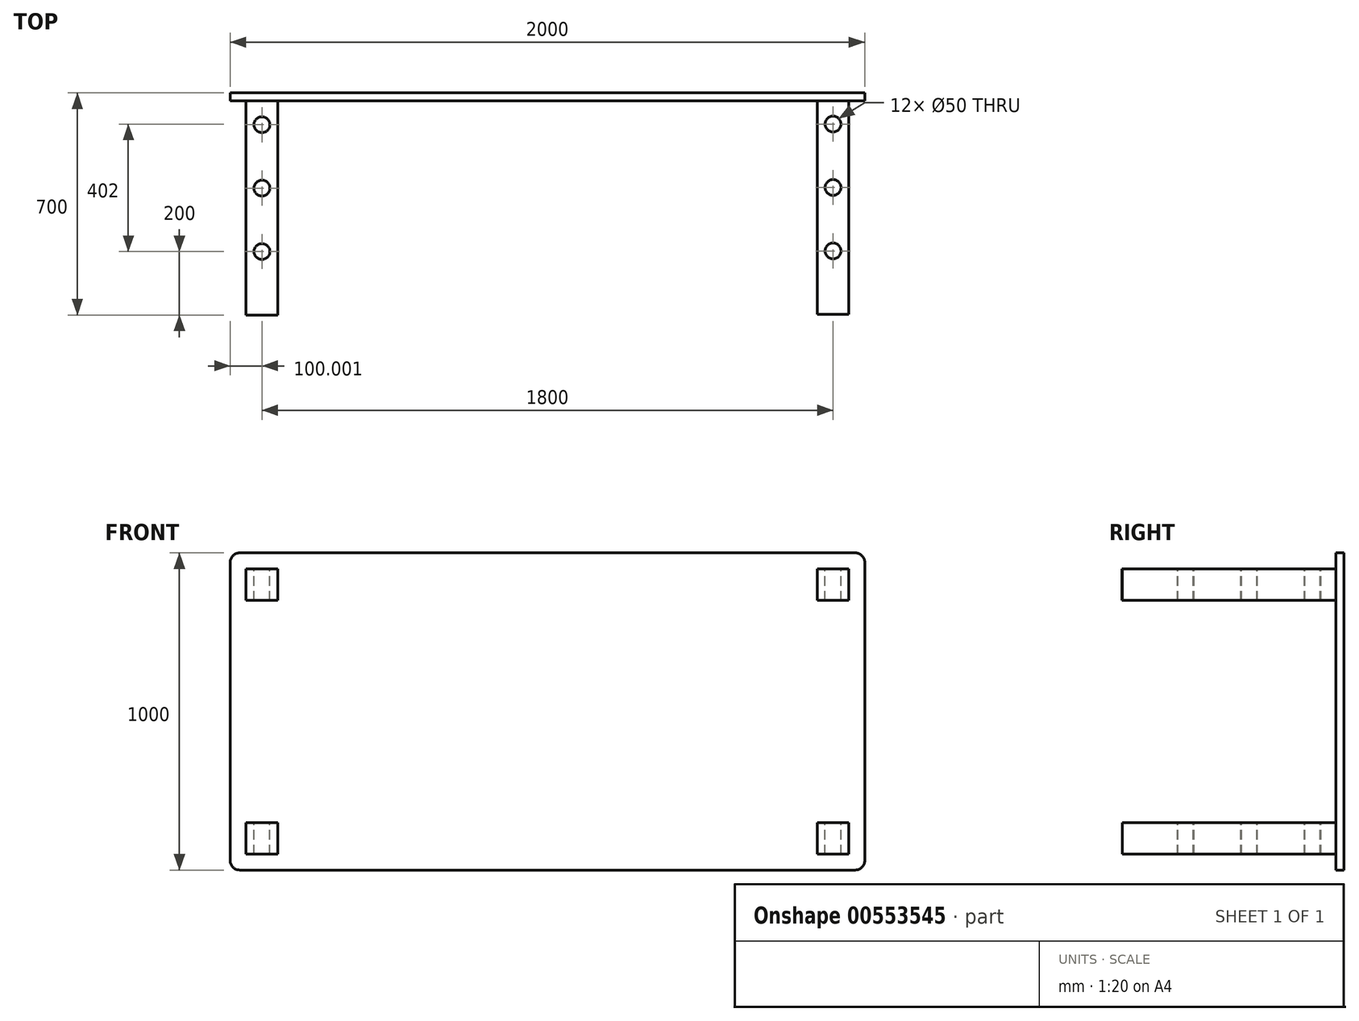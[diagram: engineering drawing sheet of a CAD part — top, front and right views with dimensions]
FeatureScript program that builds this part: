
annotation { "Feature Type Name" : "Feature", "Feature Type Description" : "" }
export const myFeature = defineFeature(function(context is Context, id is Id, definition is map)
    precondition{}
    {
        {
            var Q0;
            Q0=qCreatedBy(makeId("Front.planeOp"),FACE);
            var sketch = newSketch(context, id + "F0", { "sketchPlane" : qUnion([Q0])});
            skLineSegment(sketch, "E0.bottom", {"start": v(-998.7, 511.5) * mm, "end": v(1001.3, 511.5) * mm});
            skLineSegment(sketch, "E0.top", {"start": v(-998.7, -488.5) * mm, "end": v(1001.3, -488.5) * mm});
            skLineSegment(sketch, "E0.left", {"start": v(-998.7, 511.5) * mm, "end": v(-998.7, -488.5) * mm});
            skLineSegment(sketch, "E0.right", {"start": v(1001.3, 511.5) * mm, "end": v(1001.3, -488.5) * mm});
            skSolve(sketch);
        }
        {
            var Q0;
            Q0 = qSketchRegion(id + "F0", true);
            extrude(context, id + "F1", {"entities" : qUnion([Q0]), "depth" : 25 * mm, "offsetDistance" : 25 * mm});
        }
        {
            var Q0;
            Q0=qCreatedBy(makeId("Front.planeOp"),FACE);
            var sketch = newSketch(context, id + "F2", { "sketchPlane" : qUnion([Q0])});
            skLineSegment(sketch, "E1.bottom", {"start": v(-948.7, 461.5) * mm, "end": v(-848.7, 461.5) * mm});
            skLineSegment(sketch, "E1.top", {"start": v(-948.7, 361.5) * mm, "end": v(-848.7, 361.5) * mm});
            skLineSegment(sketch, "E1.left", {"start": v(-948.7, 461.5) * mm, "end": v(-948.7, 361.5) * mm});
            skLineSegment(sketch, "E1.right", {"start": v(-848.7, 461.5) * mm, "end": v(-848.7, 361.5) * mm});
            skSolve(sketch);
        }
        {
            var Q0;
            Q0 = qSketchRegion(id + "F2", true);
            extrude(context, id + "F3", {"entities" : qUnion([Q0]), "operationType" : NewBodyOperationType.ADD, "depth" : 700 * mm, "offsetDistance" : 25 * mm});
        }
        {
            var Q0;
            Q0=makeQuery(id+"F3.opExtrude","SWEPT_FACE",FACE,{"disambiguationData":[OSD([sQuery(id+"F2.wireOp",EDGE,"E1.bottom")])]});
            var sketch = newSketch(context, id + "F4", { "sketchPlane" : qUnion([Q0])});
            skCircle(sketch, "E2", {"center": v(-898.7, -500) * mm, "radius": 25 * mm});
            skSolve(sketch);
        }
        {
            var Q0;
            Q0=makeQuery(id+"F1.opExtrude","CAP_FACE",FACE,{"disambiguationData":[OSD([sQuery(id+"F0.wireOp",EDGE,"E0.bottom"),sQuery(id+"F0.wireOp",EDGE,"E0.top"),sQuery(id+"F0.wireOp",EDGE,"E0.left"),sQuery(id+"F0.wireOp",EDGE,"E0.right")])],"isStart":false});
            var sketch = newSketch(context, id + "F5", { "sketchPlane" : qUnion([Q0])});
            skLineSegment(sketch, "E3.bottom", {"start": v(951.3, 461.5) * mm, "end": v(851.3, 461.5) * mm});
            skLineSegment(sketch, "E3.top", {"start": v(951.3, 361.5) * mm, "end": v(851.3, 361.5) * mm});
            skLineSegment(sketch, "E3.left", {"start": v(951.3, 461.5) * mm, "end": v(951.3, 361.5) * mm});
            skLineSegment(sketch, "E3.right", {"start": v(851.3, 461.5) * mm, "end": v(851.3, 361.5) * mm});
            skLineSegment(sketch, "E4.bottom", {"start": v(-948.7, -438.5) * mm, "end": v(-848.7, -438.5) * mm});
            skLineSegment(sketch, "E4.top", {"start": v(-948.7, -338.5) * mm, "end": v(-848.7, -338.5) * mm});
            skLineSegment(sketch, "E4.left", {"start": v(-948.7, -438.5) * mm, "end": v(-948.7, -338.5) * mm});
            skLineSegment(sketch, "E4.right", {"start": v(-848.7, -438.5) * mm, "end": v(-848.7, -338.5) * mm});
            skLineSegment(sketch, "E5.bottom", {"start": v(951.3, -438.5) * mm, "end": v(851.3, -438.5) * mm});
            skLineSegment(sketch, "E5.top", {"start": v(951.3, -338.5) * mm, "end": v(851.3, -338.5) * mm});
            skLineSegment(sketch, "E5.left", {"start": v(951.3, -438.5) * mm, "end": v(951.3, -338.5) * mm});
            skLineSegment(sketch, "E5.right", {"start": v(851.3, -438.5) * mm, "end": v(851.3, -338.5) * mm});
            skSolve(sketch);
        }
        {
            var Q0;
            Q0=makeQuery(id+"F5.imprint","IMPRINT",FACE,{"disambiguationData":[TD([[makeQuery(id+"F5.imprint","IMPRINT",EDGE,{"derivedFrom":sQuery(id+"F5.wireOp",EDGE,"E4.bottom")}),1.0]])]});
            var Q1;
            Q1=makeQuery(id+"F5.imprint","IMPRINT",FACE,{"disambiguationData":[TD([[makeQuery(id+"F5.imprint","IMPRINT",EDGE,{"derivedFrom":sQuery(id+"F5.wireOp",EDGE,"E5.bottom")}),-1.0]])]});
            var Q2;
            Q2=makeQuery(id+"F5.imprint","IMPRINT",FACE,{"disambiguationData":[TD([[makeQuery(id+"F5.imprint","IMPRINT",EDGE,{"derivedFrom":sQuery(id+"F5.wireOp",EDGE,"E3.bottom")}),1.0]])]});
            extrude(context, id + "F6", {"entities" : qUnion([Q0, Q1, Q2]), "operationType" : NewBodyOperationType.ADD, "depth" : 673 * mm, "offsetDistance" : 25 * mm});
        }
        {
            var Q0;
            Q0=sQuery(id+"F4.wireOp",VERTEX,"E2.center");
            var Q1;
            Q1=makeQuery(id+"F1.opExtrude","SWEPT_BODY",BODY,{"disambiguationData":[OSD([sQuery(id+"F0.wireOp",EDGE,"E0.bottom"),sQuery(id+"F0.wireOp",EDGE,"E0.top"),sQuery(id+"F0.wireOp",EDGE,"E0.left"),sQuery(id+"F0.wireOp",EDGE,"E0.right")])]});
            hole(context, id + "F7", {"style" : HoleStyle.SIMPLE, "endStyle" : HoleEndStyle.THROUGH, "holeDiameter" : 50 * mm, "isTappedThrough" : true, "tappedDepth" : 12 * mm, "tapClearance" : 3, "locations" : qUnion([Q0]), "scope" : qUnion([Q1])});
        }
        {
            var Q0;
            Q0=makeQuery(id+"F3.opExtrude","SWEPT_FACE",FACE,{"disambiguationData":[OSD([sQuery(id+"F2.wireOp",EDGE,"E1.bottom")])]});
            var sketch = newSketch(context, id + "F8", { "sketchPlane" : qUnion([Q0])});
            skCircle(sketch, "E6", {"center": v(-898.7, -300) * mm, "radius": 25 * mm});
            skCircle(sketch, "E7", {"center": v(-898.7, -100) * mm, "radius": 25 * mm});
            skCircle(sketch, "E8", {"center": v(-898.7, -500) * mm, "radius": 25 * mm});
            skCircle(sketch, "E9", {"center": v(901.3, -498) * mm, "radius": 25 * mm});
            skCircle(sketch, "E10", {"center": v(901.3, -298) * mm, "radius": 25 * mm});
            skCircle(sketch, "E11", {"center": v(901.3, -98) * mm, "radius": 25 * mm});
            skSolve(sketch);
        }
        {
            var Q0;
            Q0 = qSketchRegion(id + "F8", true);
            extrude(context, id + "F9", {"entities" : qUnion([Q0]), "operationType" : NewBodyOperationType.ADD, "depth" : 25 * mm, "offsetDistance" : 25 * mm});
        }
        {
            var Q0;
            Q0=makeQuery(id+"F9.opExtrude","CAP_FACE",FACE,{"disambiguationData":[OSD([sQuery(id+"F8.wireOp",EDGE,"E6")])],"isStart":false});
            var Q1;
            Q1=makeQuery(id+"F9.opExtrude","CAP_FACE",FACE,{"disambiguationData":[OSD([sQuery(id+"F8.wireOp",EDGE,"E7")])],"isStart":false});
            var Q2;
            Q2=makeQuery(id+"F9.opExtrude","CAP_FACE",FACE,{"disambiguationData":[OSD([sQuery(id+"F8.wireOp",EDGE,"E8")])],"isStart":false});
            var Q3;
            Q3=makeQuery(id+"F9.opExtrude","CAP_FACE",FACE,{"disambiguationData":[OSD([sQuery(id+"F8.wireOp",EDGE,"E11")])],"isStart":false});
            var Q4;
            Q4=makeQuery(id+"F9.opExtrude","CAP_FACE",FACE,{"disambiguationData":[OSD([sQuery(id+"F8.wireOp",EDGE,"E10")])],"isStart":false});
            var Q5;
            Q5=makeQuery(id+"F9.opExtrude","CAP_FACE",FACE,{"disambiguationData":[OSD([sQuery(id+"F8.wireOp",EDGE,"E9")])],"isStart":false});
            extrude(context, id + "F10", {"entities" : qUnion([Q0, Q1, Q2, Q3, Q4, Q5]), "operationType" : NewBodyOperationType.REMOVE, "endBound" : BoundingType.THROUGH_ALL, "oppositeDirection" : true, "depth" : 25 * mm, "offsetDistance" : 25 * mm});
        }
        {
            var Q0;
            Q0=makeQuery(id+"F1.opExtrude","SWEPT_EDGE",EDGE,{"disambiguationData":[OSD([sQuery(id+"F0.wireOp",EDGE,"E0.bottom"),sQuery(id+"F0.wireOp",EDGE,"E0.left")])]});
            var Q1;
            Q1=makeQuery(id+"F1.opExtrude","SWEPT_EDGE",EDGE,{"disambiguationData":[OSD([sQuery(id+"F0.wireOp",EDGE,"E0.top"),sQuery(id+"F0.wireOp",EDGE,"E0.left")])]});
            var Q2;
            Q2=makeQuery(id+"F1.opExtrude","SWEPT_EDGE",EDGE,{"disambiguationData":[OSD([sQuery(id+"F0.wireOp",EDGE,"E0.top"),sQuery(id+"F0.wireOp",EDGE,"E0.right")])]});
            var Q3;
            Q3=makeQuery(id+"F1.opExtrude","SWEPT_EDGE",EDGE,{"disambiguationData":[OSD([sQuery(id+"F0.wireOp",EDGE,"E0.bottom"),sQuery(id+"F0.wireOp",EDGE,"E0.right")])]});
            fillet(context, id + "F11", {"entities" : qUnion([Q0, Q1, Q2, Q3]), "radius" : 30 * mm, "tangentPropagation" : true, "allowEdgeOverflow" : false});
        }
    });
